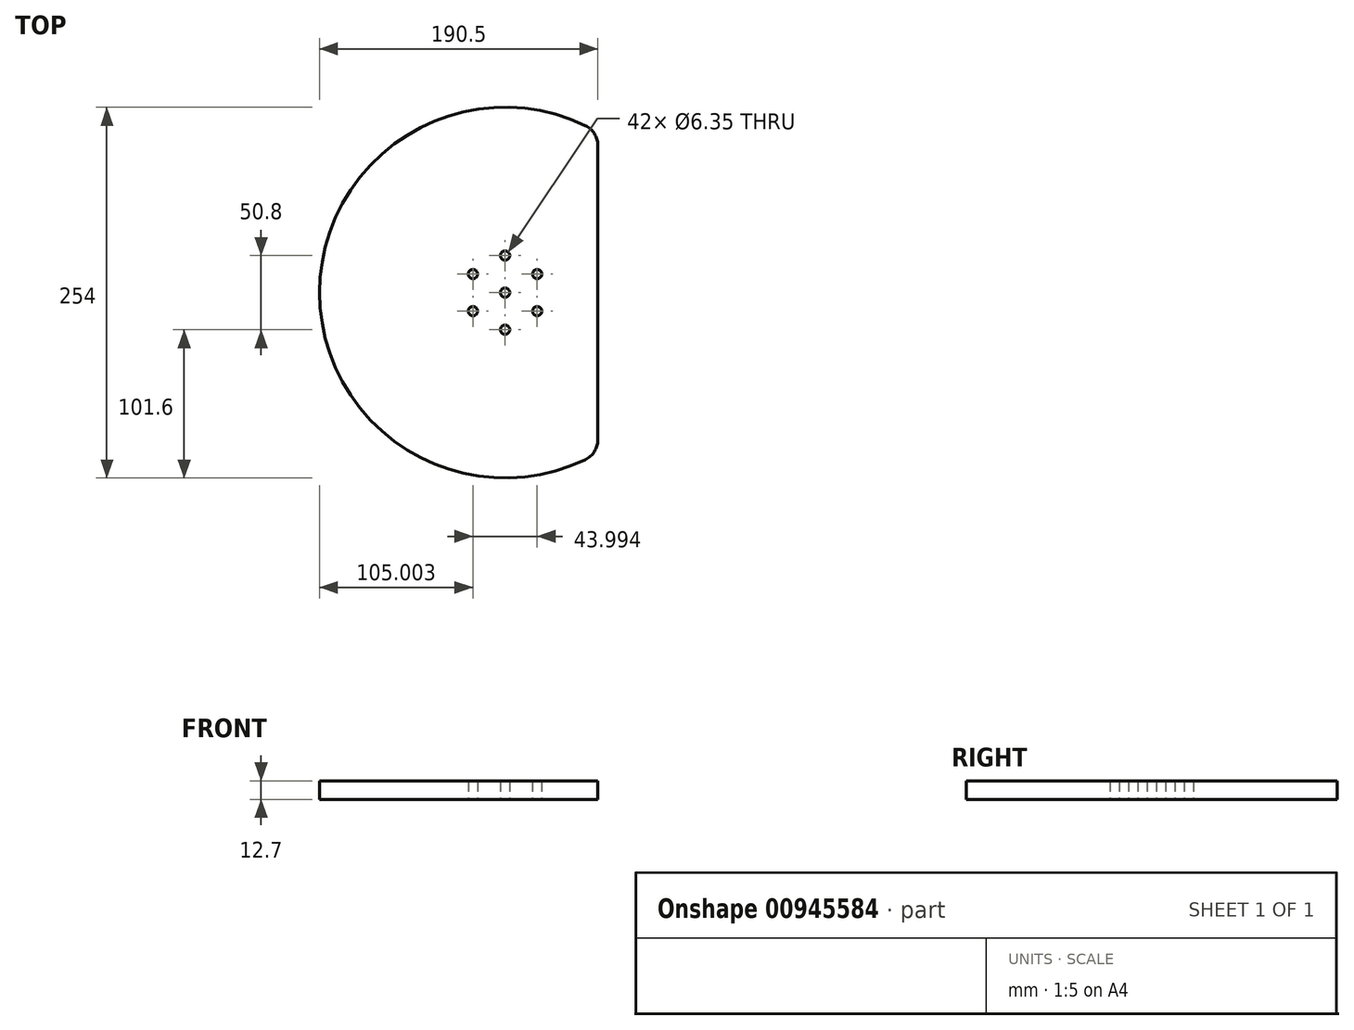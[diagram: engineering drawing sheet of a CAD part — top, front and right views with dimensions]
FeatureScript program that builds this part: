
annotation { "Feature Type Name" : "Feature", "Feature Type Description" : "" }
export const myFeature = defineFeature(function(context is Context, id is Id, definition is map)
    precondition{}
    {
        {
            var Q0;
            Q0=qCreatedBy(makeId("Top.planeOp"),FACE);
            var sketch = newSketch(context, id + "F0", { "sketchPlane" : qUnion([Q0])});
            skCircle(sketch, "E0", {"center": v(0, 0) * mm, "radius": 127 * mm});
            skLineSegment(sketch, "E1", {"start": v(88.9, 90.7) * mm, "end": v(88.9, -90.7) * mm});
            skLineSegment(sketch, "E2", {"start": v(88.9, 0) * mm, "end": v(127, 0) * mm});
            skSolve(sketch);
        }
        {
            var Q0;
            Q0=qCreatedBy(makeId("Top.planeOp"),FACE);
            var sketch = newSketch(context, id + "F1", { "sketchPlane" : qUnion([Q0])});
            skArc(sketch, "E3", {"start": v(55, 114.47) * mm, "mid": v(-127, 0) * mm, "end": v(55, -114.47) * mm});
            skLineSegment(sketch, "E4", {"start": v(63.5, 100.95) * mm, "end": v(63.5, -100.95) * mm});
            skPoint(sketch, "E5.visualSharp", {"position": v(63.5, 109.99) * mm});
            skArc(sketch, "E5.filletArc", {"start": v(63.5, 100.95) * mm, "mid": v(61.2, 108.94) * mm, "end": v(55, 114.47) * mm});
            skPoint(sketch, "E6.visualSharp", {"position": v(63.5, -109.99) * mm});
            skArc(sketch, "E6.filletArc", {"start": v(55, -114.47) * mm, "mid": v(61.2, -108.94) * mm, "end": v(63.5, -100.95) * mm});
            skSolve(sketch);
        }
        {
            var Q0;
            Q0=makeQuery(id+"F1.imprint","IMPRINT",FACE,{"disambiguationData":[TD([[makeQuery(id+"F1.imprint","IMPRINT",EDGE,{"derivedFrom":sQuery(id+"F1.wireOp",EDGE,"E3")}),1.0]])]});
            extrude(context, id + "F2", {"entities" : qUnion([Q0]), "depth" : 12.7 * mm, "offsetDistance" : 25 * mm});
        }
        {
            var Q0;
            Q0=qCreatedBy(makeId("Top.planeOp"),FACE);
            var sketch = newSketch(context, id + "F3", { "sketchPlane" : qUnion([Q0])});
            skCircle(sketch, "E7", {"center": v(0, 0) * mm, "radius": 3.17 * mm});
            skCircle(sketch, "E8.cCircle", {"center": v(0, 0) * mm, "radius": 25.4 * mm, "construction": true});
            skLineSegment(sketch, "E8.0", {"start": v(0, -25.4) * mm, "end": v(-22, -12.7) * mm, "construction": true});
            skLineSegment(sketch, "E8.1", {"start": v(-22, -12.7) * mm, "end": v(-22, 12.7) * mm, "construction": true});
            skLineSegment(sketch, "E8.2", {"start": v(-22, 12.7) * mm, "end": v(0, 25.4) * mm, "construction": true});
            skLineSegment(sketch, "E8.3", {"start": v(0, 25.4) * mm, "end": v(22, 12.7) * mm, "construction": true});
            skLineSegment(sketch, "E8.4", {"start": v(22, 12.7) * mm, "end": v(22, -12.7) * mm, "construction": true});
            skLineSegment(sketch, "E8.5", {"start": v(22, -12.7) * mm, "end": v(0, -25.4) * mm, "construction": true});
            skCircle(sketch, "E9", {"center": v(0, 25.4) * mm, "radius": 3.18 * mm});
            skCircle(sketch, "E10.1.0", {"center": v(-22, 12.7) * mm, "radius": 3.18 * mm});
            skCircle(sketch, "E10.2.0", {"center": v(-22, -12.7) * mm, "radius": 3.18 * mm});
            skCircle(sketch, "E10.3.0", {"center": v(0, -25.4) * mm, "radius": 3.18 * mm});
            skCircle(sketch, "E10.4.0", {"center": v(22, -12.7) * mm, "radius": 3.18 * mm});
            skCircle(sketch, "E10.5.0", {"center": v(22, 12.7) * mm, "radius": 3.18 * mm});
            skSolve(sketch);
        }
        {
            var Q0;
            Q0=qSketchRegion(id+"F3",true);
            var Q1;
            Q1=makeQuery(id+"F2.opExtrude","CAP_FACE",FACE,{"disambiguationData":[OSD([sQuery(id+"F1.wireOp",EDGE,"E3"),sQuery(id+"F1.wireOp",EDGE,"E4"),sQuery(id+"F1.wireOp",EDGE,"E5.filletArc"),sQuery(id+"F1.wireOp",EDGE,"E6.filletArc")])],"isStart":false});
            extrude(context, id + "F4", {"entities" : qUnion([Q0]), "operationType" : NewBodyOperationType.REMOVE, "endBound" : BoundingType.UP_TO_SURFACE, "depth" : 25 * mm, "endBoundEntityFace" : qUnion([Q1]), "offsetDistance" : 25 * mm});
        }
    });
